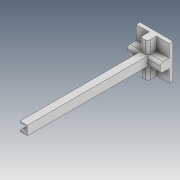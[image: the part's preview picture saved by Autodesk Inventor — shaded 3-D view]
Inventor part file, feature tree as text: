
AUTODESK INVENTOR PART (.ipt)
format: ipt  version: 2021 (Build 250183000, 183)  size: 178,176 bytes
history: native  units: in
note: dims shown in document units (in); Inventor stores cm internally (conversion verified against a paired STEP export)
features: sketch x8, extrude x7, fillet x2, other x1
ambient origin geometry x8: Origin, YZ Plane, XZ Plane, XY Plane, X Axis, Y Axis, Z Axis, Center Point
bodies: Body1 (feature_tree)
feature tree (18):
  other  "Sólido1"
  sketch  "Esboço1"  dims[d0=0.2835in d1=0.0394in]
  extrude  "Extrusão1"  Depth=0.0394in
  extrude  "Extrusão2"  Depth=0.187in
  extrude  "Extrusão3"  Depth=4.1339in TaperAngle=0.0deg
  extrude  "Extrusão4"  Depth=0.3937in TaperAngle=0.0deg
  extrude  "Extrusão5"  Depth=0.3937in TaperAngle=0.0deg
  fillet  "Arredondamento1"  Radius=0.1181in
  extrude  "Extrusão6"  Depth=0.0787in
  extrude  "Extrusão7"  Depth=0.4035in TaperAngle=0.0deg
  fillet  "Arredondamento2"  Radius=0.0787in
  sketch  "Esboço2"  dims[d2=0.2264in d3=0.187in]
  sketch  "Esboço3"  dims[d4=0.2047in d5=4.1339in d6=0.0in]
  sketch  "Esboço4"  dims[d7=0.3937in d8=0.3937in d9=0.0in]
  sketch  "Esboço5"  dims[d10=0.3937in d11=0.0in d12=0.3937in d13=0.0in d14=0.1181in]
  sketch  "Esboço6"  dims[d15=0.3937in d16=0.0in d17=0.0787in]
  sketch  "Esboço7"  dims[d18=0.5906in d19=0.0in d20=0.4035in d21=0.0in d22=0.0787in]
  sketch  "Esboço8"
